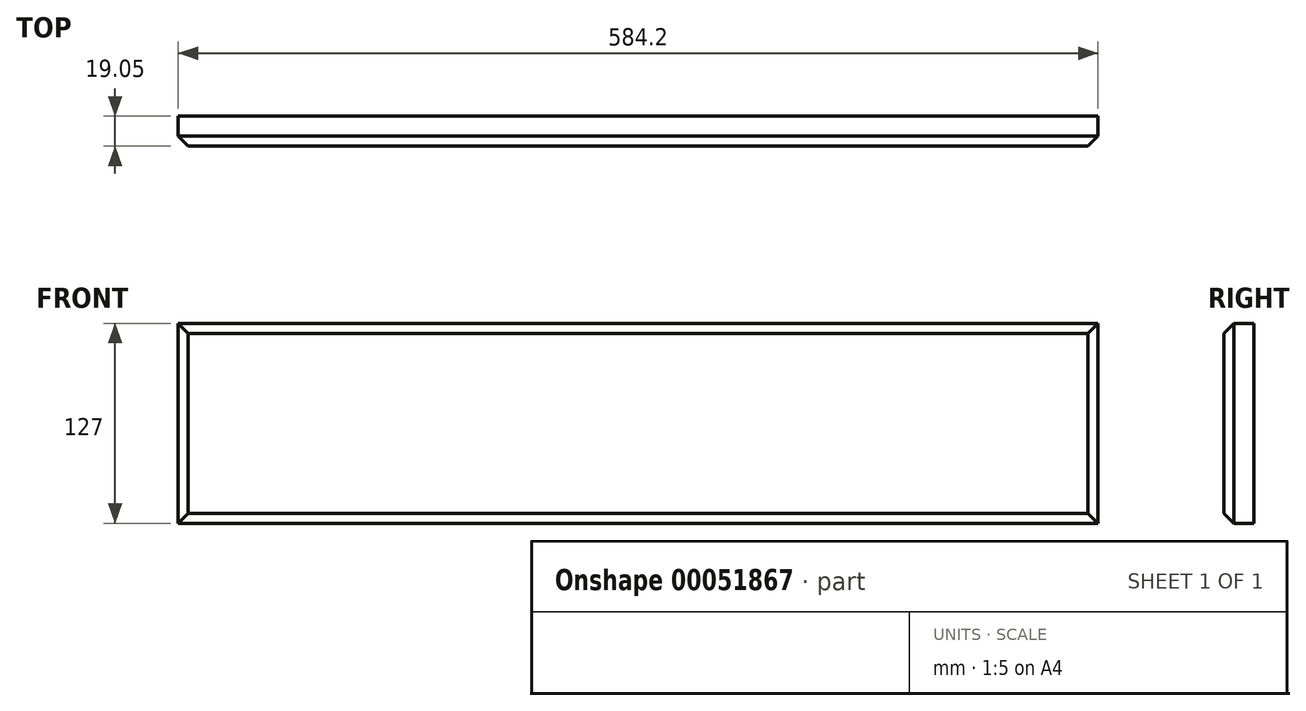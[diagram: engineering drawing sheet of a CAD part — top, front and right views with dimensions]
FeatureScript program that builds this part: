
annotation { "Feature Type Name" : "Feature", "Feature Type Description" : "" }
export const myFeature = defineFeature(function(context is Context, id is Id, definition is map)
    precondition{}
    {
        {
            var Q0;
            Q0=qCreatedBy(makeId("Front.planeOp"),FACE);
            var sketch = newSketch(context, id + "F0", { "sketchPlane" : qUnion([Q0])});
            skLineSegment(sketch, "E0.bottom", {"start": v(-292.1, 63.5) * mm, "end": v(292.1, 63.5) * mm});
            skLineSegment(sketch, "E0.top", {"start": v(-292.1, -63.5) * mm, "end": v(292.1, -63.5) * mm});
            skLineSegment(sketch, "E0.left", {"start": v(-292.1, 63.5) * mm, "end": v(-292.1, -63.5) * mm});
            skLineSegment(sketch, "E0.right", {"start": v(292.1, 63.5) * mm, "end": v(292.1, -63.5) * mm});
            skSolve(sketch);
        }
        {
            var Q0;
            Q0=makeQuery(id+"F0.imprint","IMPRINT",FACE,{"disambiguationData":[TD([[makeQuery(id+"F0.imprint","IMPRINT",EDGE,{"derivedFrom":sQuery(id+"F0.wireOp",EDGE,"E0.bottom")}),-1.0]])]});
            extrude(context, id + "F1", {"entities" : qUnion([Q0]), "depth" : 19.05 * mm});
        }
        {
            var Q0;
            Q0=makeQuery(id+"F1.opExtrude","CAP_EDGE",EDGE,{"disambiguationData":[OSD([sQuery(id+"F0.wireOp",EDGE,"E0.right")])],"isStart":false});
            var Q1;
            Q1=makeQuery(id+"F1.opExtrude","CAP_EDGE",EDGE,{"disambiguationData":[OSD([sQuery(id+"F0.wireOp",EDGE,"E0.left")])],"isStart":false});
            var Q2;
            Q2=makeQuery(id+"F1.opExtrude","CAP_EDGE",EDGE,{"disambiguationData":[OSD([sQuery(id+"F0.wireOp",EDGE,"E0.bottom")])],"isStart":false});
            var Q3;
            Q3=makeQuery(id+"F1.opExtrude","CAP_EDGE",EDGE,{"disambiguationData":[OSD([sQuery(id+"F0.wireOp",EDGE,"E0.top")])],"isStart":false});
            chamfer(context, id + "F2", {"entities" : qUnion([Q0, Q1, Q2, Q3]), "width" : 6.35 * mm, "tangentPropagation" : true});
        }
    });
